# Revit family: QF_BOURGEAT_Self_meuble_dessus_verre_trempe
name_source: partatom
category: Equipement spécialisé
revit_build: Autodesk Revit 2015 (Build: 20140606_1530(x64)
units: mm (PartAtom-declared; Revit-internal decimal feet)

## types (55) — shared parameters
Certification = NF alimentaire
Charge max = 200.00 kg
Fabricant = BOURGEAT
Fréquence = 50 Hz
Indice de protection = 21
Nature isolant = Laine de verre
Phase = 2
Profondeur hors tout = 820 mm
Spécification du Fabricant = Meuble dessus verre trempé OASIS
Tension = 230 V
URL catalogue = http://www.bourgeat.fr

## per-type parameters (varying)
| type | Etageres | Hauteur hors tout | Intensité nominale | Longueur hors tout | Modèle | Pieds | Poids net à vide | Presentoir | Puissance électrique  | Roues | lg_etagere | lg_porte | lg_presentoir | lgconsole | lgmeuble |
| GN6_baie_libre | Non | 900 mm | 11 A | 2184 mm  [stored 7.16535 ft] | 851026 | Oui | 210.00 kg | Non | 2610 W | Non | 1712 mm  [stored 5.6168 ft] | 866 mm | 2072 mm | 2140 mm  [stored 7.021 ft] | 2116 mm |
| GN6_baie_libre+presentoir_neutre | Non | 1330 mm | 11 A | 2184 mm  [stored 7.16535 ft] | 851026+851316 | Oui | 240.00 kg | Oui | 2610 W | Non | 1712 mm  [stored 5.6168 ft] | 866 mm | 2072 mm | 2140 mm  [stored 7.021 ft] | 2116 mm |
| GN6_baie_libre+presentoir_chauffant | Non | 1330 mm | 16 A | 2184 mm  [stored 7.16535 ft] | 851026+851306 | Oui | 240.00 kg | Oui | 3570 W | Non | 1712 mm  [stored 5.6168 ft] | 866 mm | 2072 mm | 2140 mm  [stored 7.021 ft] | 2116 mm |
| GN6_baie_libre+roues | Non | 900 mm | 11 A | 2184 mm  [stored 7.16535 ft] | 851026+854950 | Non | 210.00 kg | Non | 2610 W | Oui | 1712 mm  [stored 5.6168 ft] | 866 mm | 2072 mm | 2140 mm  [stored 7.021 ft] | 2116 mm |
| GN6_baie_libre+etageres | Oui | 900 mm | 11 A | 2184 mm  [stored 7.16535 ft] | 851026+854906 | Oui | 210.00 kg | Non | 2610 W | Non | 1712 mm  [stored 5.6168 ft] | 866 mm | 2072 mm | 2140 mm  [stored 7.021 ft] | 2116 mm |
| GN6_baie_libre+presentoir_neutre+roues | Non | 1330 mm | 11 A | 2184 mm  [stored 7.16535 ft] | 851026+851316+854950 | Non | 240.00 kg | Oui | 2610 W | Oui | 1712 mm  [stored 5.6168 ft] | 866 mm | 2072 mm | 2140 mm  [stored 7.021 ft] | 2116 mm |
| GN6_baie_libre+presentoir_neutre+etageres | Oui | 1330 mm | 11 A | 2184 mm  [stored 7.16535 ft] | 851026+851316+854946 | Oui | 240.00 kg | Oui | 2610 W | Non | 1712 mm  [stored 5.6168 ft] | 866 mm | 2072 mm | 2140 mm  [stored 7.021 ft] | 2116 mm |
| GN6_baie_libre+presentoir_chauffant+etageres | Oui | 1330 mm | 16 A | 2184 mm  [stored 7.16535 ft] | 851026+851306+854946 | Oui | 240.00 kg | Oui | 3570 W | Non | 1712 mm  [stored 5.6168 ft] | 866 mm | 2072 mm | 2140 mm  [stored 7.021 ft] | 2116 mm |
| GN6_baie_libre+presentoir_chauffant+roues | Oui | 1330 mm | 16 A | 2184 mm  [stored 7.16535 ft] | 851026+851306+854950 | Non | 240.00 kg | Oui | 3570 W | Oui | 1712 mm  [stored 5.6168 ft] | 866 mm | 2072 mm | 2140 mm  [stored 7.021 ft] | 2116 mm |
| GN6_baie_libre+presentoir_chauffant+roues+etageres | Oui | 1330 mm | 16 A | 2184 mm  [stored 7.16535 ft] | 851026+851306+854950+854946 | Non | 240.00 kg | Oui | 3570 W | Oui | 1712 mm  [stored 5.6168 ft] | 866 mm | 2072 mm | 2140 mm  [stored 7.021 ft] | 2116 mm |
| GN6_baie_libre+presentoir_neutre+roues+etageres | Oui | 1330 mm | 11 A | 2184 mm  [stored 7.16535 ft] | 851026+851316+854950+854946 | Non | 240.00 kg | Oui | 2610 W | Oui | 1712 mm  [stored 5.6168 ft] | 866 mm | 2072 mm | 2140 mm  [stored 7.021 ft] | 2116 mm |
| GN5_baie_libre | Non | 900 mm | 9 A | 1859 mm | 851025 | Oui | 190.00 kg | Non | 2175 W | Non | 1387 mm | 704 mm | 1747 mm | 1815 mm | 1791 mm |
| GN5_baie_libre+roues | Non | 900 mm | 9 A | 1859 mm | 851025+854950 | Non | 190.00 kg | Non | 2175 W | Oui | 1387 mm | 704 mm | 1747 mm | 1815 mm | 1791 mm |
| GN5_baie_libre+etageres | Oui | 900 mm | 9 A | 1859 mm | 851025+854946 | Oui | 190.00 kg | Non | 2175 W | Non | 1387 mm | 704 mm | 1747 mm | 1815 mm | 1791 mm |
| GN5_baie_libre+presentoir_neutre | Non | 1330 mm | 9 A | 1859 mm | 851025+851315 | Oui | 215.00 kg | Oui | 2175 W | Non | 1387 mm | 704 mm | 1747 mm | 1815 mm | 1791 mm |
| GN5_baie_libre+presentoir_chauffant | Non | 1330 mm | 13 A | 1859 mm | 851025+851305 | Oui | 215.00 kg | Oui | 2975 W | Non | 1387 mm | 704 mm | 1747 mm | 1815 mm | 1791 mm |
| GN5_baie_libre+presentoir_neutre+roues | Non | 1330 mm | 9 A | 1859 mm | 851025+851315+854950 | Non | 215.00 kg | Oui | 2175 W | Oui | 1387 mm | 704 mm | 1747 mm | 1815 mm | 1791 mm |
| GN5_baie_libre+presentoir_neutre+etageres | Non | 1330 mm | 9 A | 1859 mm | 851025+851315+854945 | Non | 215.00 kg | Oui | 2175 W | Oui | 1387 mm | 704 mm | 1747 mm | 1815 mm | 1791 mm |
| GN5_baie_libre+presentoir_chauffant+roues | Non | 1330 mm | 13 A | 1859 mm | 851025+851305+854950 | Non | 215.00 kg | Oui | 2975 W | Oui | 1387 mm | 704 mm | 1747 mm | 1815 mm | 1791 mm |
| GN5_baie_libre+presentoir_chauffant+etageres | Oui | 1330 mm | 13 A | 1859 mm | 851025+851305+854945 | Oui | 215.00 kg | Oui | 2975 W | Non | 1387 mm | 704 mm | 1747 mm | 1815 mm | 1791 mm |
| GN5_baie_libre+presentoir_chauffant+roues+etageres | Non | 1330 mm | 13 A | 1859 mm | 851025+851305+854950+854945 | Non | 215.00 kg | Oui | 2975 W | Oui | 1387 mm | 704 mm | 1747 mm | 1815 mm | 1791 mm |
| GN5_baie_libre+presentoir_neutre+roues+etageres | Non | 1330 mm | 9 A | 1859 mm | 851025+851315+854950+854946 | Non | 215.00 kg | Oui | 2175 W | Oui | 1387 mm | 704 mm | 1747 mm | 1815 mm | 1791 mm |
| GN3_baie_libre | Non | 900 mm | 6 A | 1209 mm | 851023 | Oui | 150.00 kg | Non | 1305 W | Non | 737 mm | 379 mm | 1097 mm | 1165 mm | 1141 mm |
| GN4_baie_libre+presentoir_neutre | Non | 1330 mm | 8 A | 1534 mm | 851024+851314 | Oui | 190.00 kg | Oui | 1740 W | Non | 1062 mm | 541 mm | 1422 mm | 1490 mm | 1466 mm |
| GN4_baie_libre+presentoir_chauffant | Non | 1330 mm | 10 A | 1534 mm | 851024+851304 | Oui | 190.00 kg | Oui | 2380 W | Non | 1062 mm | 541 mm | 1422 mm | 1490 mm | 1466 mm |
| GN4_baie_libre+roues | Non | 900 mm | 8 A | 1534 mm | 851024+854950 | Non | 170.00 kg | Non | 1740 W | Oui | 1062 mm | 541 mm | 1422 mm | 1490 mm | 1466 mm |
| GN4_baie_libre+etageres | Oui | 900 mm | 8 A | 1534 mm | 851024+854944 | Oui | 170.00 kg | Non | 1740 W | Non | 1062 mm | 541 mm | 1422 mm | 1490 mm | 1466 mm |
| GN4_baie_libre+presentoir_neutre+roues | Non | 1330 mm | 8 A | 1534 mm | 851024+851314+854950 | Non | 190.00 kg | Oui | 1740 W | Oui | 1062 mm | 541 mm | 1422 mm | 1490 mm | 1466 mm |
| GN4_baie_libre+presentoir_chauffant+roues | Non | 1330 mm | 10 A | 1534 mm | 851024+851304+854950 | Non | 190.00 kg | Oui | 2380 W | Oui | 1062 mm | 541 mm | 1422 mm | 1490 mm | 1466 mm |
| GN4_baie_libre+presentoir_neutre+etegeres | Oui | 1330 mm | 8 A | 1534 mm | 851024+851314+854944 | Non | 190.00 kg | Oui | 1740 W | Oui | 1062 mm | 541 mm | 1422 mm | 1490 mm | 1466 mm |
| GN4_baie_libre+presentoir_chauffant+etageres | Oui | 1330 mm | 10 A | 1534 mm | 851024+851304+854944 | Oui | 190.00 kg | Oui | 2380 W | Non | 1062 mm | 541 mm | 1422 mm | 1490 mm | 1466 mm |
| GN4_baie_libre+presentoir_chauffant+etageres+roues | Oui | 1330 mm | 10 A | 1534 mm | 851024+851304+854944+854950 | Non | 190.00 kg | Oui | 2390 W | Oui | 1062 mm | 541 mm | 1422 mm | 1490 mm | 1466 mm |
| GN4_baie_libre+presentoir_neutre+etageres+roues | Oui | 1330 mm | 8 A | 1534 mm | 851024+851314+854944+854950 | Non | 190.00 kg | Oui | 1740 W | Oui | 1062 mm | 541 mm | 1422 mm | 1490 mm | 1466 mm |
| GN3_baie_libre+roues | Non | 900 mm | 6 A | 1209 mm | 851023+854950 | Non | 150.00 kg | Non | 1305 W | Oui | 737 mm | 379 mm | 1097 mm | 1165 mm | 1141 mm |
| GN3_baie_libre+etageres | Oui | 900 mm | 6 A | 1209 mm | 851023+854943 | Non | 150.00 kg | Non | 1305 W | Oui | 737 mm | 379 mm | 1097 mm | 1165 mm | 1141 mm |
| GN3_baie_libre+presentoir_neutre | Non | 1330 mm | 6 A | 1209 mm | 851023+851313 | Oui | 165.00 kg | Oui | 1305 W | Non | 737 mm | 379 mm | 1097 mm | 1165 mm | 1141 mm |
| GN3_baie_libre+presentoir_chauffant | Non | 1330 mm | 8 A | 1209 mm | 851023+851303 | Oui | 165.00 kg | Oui | 1785 W | Non | 737 mm | 379 mm | 1097 mm | 1165 mm | 1141 mm |
| GN3_baie_libre+presentoir_chauffant+roues | Non | 1330 mm | 8 A | 1209 mm | 851023+851303+854950 | Non | 165.00 kg | Oui | 1785 W | Oui | 737 mm | 379 mm | 1097 mm | 1165 mm | 1141 mm |
| GN3_baie_libre+presentoir_chauffant+etageres | Oui | 1330 mm | 8 A | 1209 mm | 851023+851303+854943 | Oui | 165.00 kg | Oui | 1305 W | Non | 737 mm | 379 mm | 1097 mm | 1165 mm | 1141 mm |
| GN3_baie_libre+presentoir_neutre+roues | Non | 1330 mm | 6 A | 1209 mm | 851023+851313+854950 | Non | 165.00 kg | Oui | 1305 W | Oui | 737 mm | 379 mm | 1097 mm | 1165 mm | 1141 mm |
| GN3_baie_libre+presentoir_neutre+etageres | Oui | 1330 mm | 6 A | 1209 mm | 851023+851313+854943 | Oui | 165.00 kg | Oui | 1305 W | Non | 737 mm | 379 mm | 1097 mm | 1165 mm | 1141 mm |
| GN3_baie_libre+presentoir_neutre+roues+etageres | Oui | 1330 mm | 6 A | 1209 mm | 851023+851313+854950+854943 | Non | 165.00 kg | Oui | 1305 W | Oui | 737 mm | 379 mm | 1097 mm | 1165 mm | 1141 mm |
| GN3_baie_libre+presentoir_chauffant+roues+etageres | Oui | 1330 mm | 8 A | 1209 mm | 851023+851303+854950+854943 | Non | 165.00 kg | Oui | 1785 W | Oui | 737 mm | 379 mm | 1097 mm | 1165 mm | 1141 mm |
| GN2_baie_libre | Non | 900 mm | 4 A | 884 mm  [stored 2.90026 ft] | 851022 | Oui | 130.00 kg | Non | 870 W | Non | 412 mm  [stored 1.35171 ft] | 216 mm | 772 mm  [stored 2.53281 ft] | 840 mm  [stored 2.75591 ft] | 816 mm |
| GN2_baie_libre+roues | Non | 900 mm | 4 A | 884 mm  [stored 2.90026 ft] | 851022+854950 | Non | 130.00 kg | Non | 870 W | Oui | 412 mm  [stored 1.35171 ft] | 216 mm | 772 mm  [stored 2.53281 ft] | 840 mm  [stored 2.75591 ft] | 816 mm |
| GN2_baie_libre+etageres | Oui | 900 mm | 4 A | 884 mm  [stored 2.90026 ft] | 851022+854942 | Oui | 130.00 kg | Non | 870 W | Non | 412 mm  [stored 1.35171 ft] | 216 mm | 772 mm  [stored 2.53281 ft] | 840 mm  [stored 2.75591 ft] | 816 mm |
| GN2_baie_libre+presentoir_chauffant | Oui | 1330 mm | 5 A | 884 mm  [stored 2.90026 ft] | 851022+851302 | Oui | 140.00 kg | Non | 1190 W | Non | 412 mm  [stored 1.35171 ft] | 216 mm | 772 mm  [stored 2.53281 ft] | 840 mm  [stored 2.75591 ft] | 816 mm |
| GN2_baie_libre+presentoir_chauffant+roues | Non | 1330 mm | 5 A | 884 mm  [stored 2.90026 ft] | 851022+851302+854950 | Non | 140.00 kg | Oui | 1190 W | Oui | 412 mm  [stored 1.35171 ft] | 216 mm | 772 mm  [stored 2.53281 ft] | 840 mm  [stored 2.75591 ft] | 816 mm |
| GN2_baie_libre+presentoir_chauffant+etageres | Oui | 1330 mm | 5 A | 884 mm  [stored 2.90026 ft] | 851022+851302+854942 | Oui | 140.00 kg | Oui | 1190 W | Non | 412 mm  [stored 1.35171 ft] | 216 mm | 772 mm  [stored 2.53281 ft] | 840 mm  [stored 2.75591 ft] | 816 mm |
| GN2_baie_libre+presentoir_chauffant+roues+etageres | Non | 1330 mm | 5 A | 884 mm  [stored 2.90026 ft] | 851022+851302+854950+854942 | Non | 140.00 kg | Oui | 1190 W | Oui | 412 mm  [stored 1.35171 ft] | 216 mm | 772 mm  [stored 2.53281 ft] | 840 mm  [stored 2.75591 ft] | 816 mm |
| GN2_baie_libre+roues+etageres | Oui | 900 mm | 4 A | 884 mm  [stored 2.90026 ft] | 851022+854950+854942 | Non | 130.00 kg | Non | 870 W | Oui | 412 mm  [stored 1.35171 ft] | 216 mm | 772 mm  [stored 2.53281 ft] | 840 mm  [stored 2.75591 ft] | 816 mm |
| GN3_baie_libre+roues+etageres | Non | 900 mm | 6 A | 1209 mm | 851023+854950+854943 | Non | 150.00 kg | Non | 1305 W | Oui | 737 mm | 379 mm | 1097 mm | 1165 mm | 1141 mm |
| GN4_baie_libre | Non | 900 mm | 8 A | 1534 mm | 851024 | Oui | 170.00 kg | Non | 1740 W | Non | 1062 mm | 541 mm | 1422 mm | 1490 mm | 1466 mm |
| GN5_baie_libre+roues+etageres | Oui | 900 mm | 9 A | 1859 mm | 851025+854950+854945 | Non | 190.00 kg | Non | 2175 W | Oui | 1387 mm | 704 mm | 1747 mm | 1815 mm | 1791 mm |
| GN6_baie_libre+roues+etageres | Oui | 900 mm | 11 A | 2184 mm  [stored 7.16535 ft] | 851026+854950+854946 | Non | 210.00 kg | Non | 2610 W | Oui | 1712 mm  [stored 5.6168 ft] | 866 mm | 2072 mm | 2140 mm  [stored 7.021 ft] | 2116 mm |

note: [stored X ft] marks values corroborated as IEEE doubles in the binary element streams (Revit-internal decimal feet)

## geometry (parser evidence)
native form markers: Blend x12
no freeform markers — native parametric forms only
